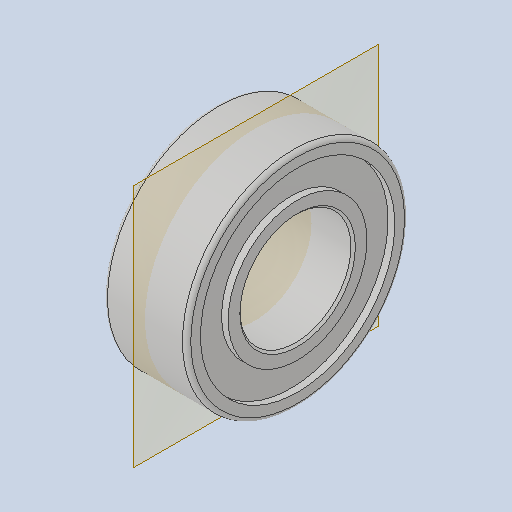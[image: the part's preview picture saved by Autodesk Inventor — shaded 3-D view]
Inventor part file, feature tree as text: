
AUTODESK INVENTOR PART (.ipt)
format: ipt  version: 2023.3 (Build 273359000, 359)  size: 168,960 bytes
history: native  units: in
note: dims shown in document units (in); Inventor stores cm internally (conversion verified against a paired STEP export)
features: chamfer x1
ambient origin geometry x8: Origin, YZ Plane, XZ Plane, XY Plane, X Axis, Y Axis, Z Axis, Center Point
bodies: Solid1 (feature_tree)
feature tree (1):
  chamfer  "Chamfer1"  [1 undecoded]
note: 1 required parameter value undecoded (feature->parameter linkage not recoverable at this tier; creation-order binding heuristic only, values carry confidence <= 0.55)
